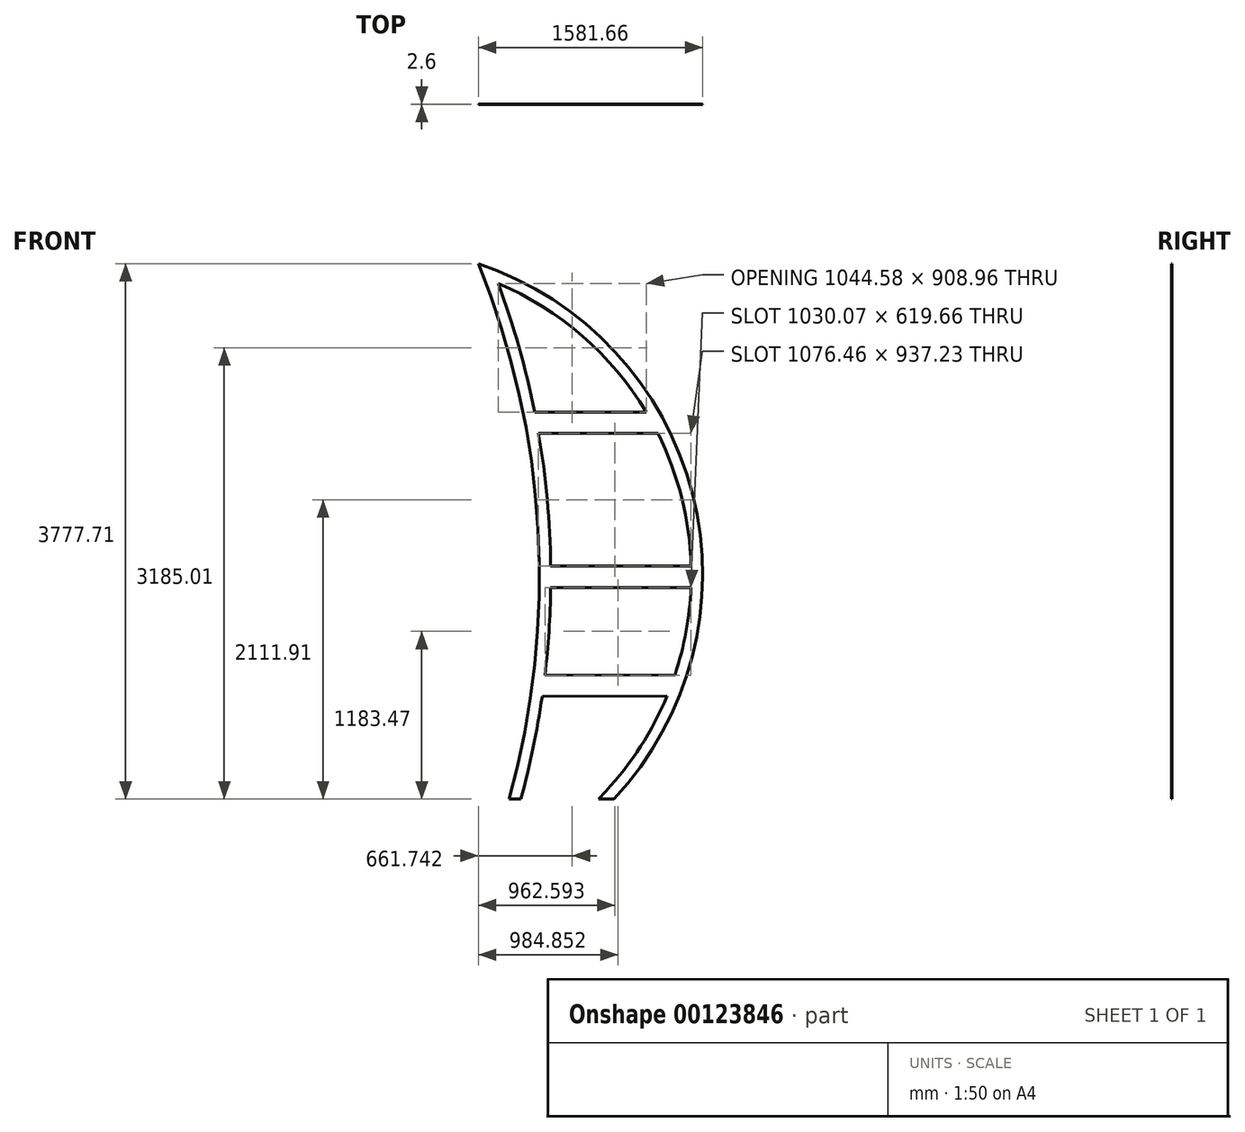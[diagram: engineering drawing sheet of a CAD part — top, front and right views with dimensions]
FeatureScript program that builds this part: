
annotation { "Feature Type Name" : "Feature", "Feature Type Description" : "" }
export const myFeature = defineFeature(function(context is Context, id is Id, definition is map)
    precondition{}
    {
        {
            var Q0;
            Q0=qCreatedBy(makeId("Front.planeOp"),FACE);
            var sketch = newSketch(context, id + "F0", { "sketchPlane" : qUnion([Q0])});
            skArc(sketch, "E0", {"start": v(-809.64, -1060.94) * mm, "mid": v(-605.41, 845.86) * mm, "end": v(-1026.5, 2716.77) * mm});
            skArc(sketch, "E1", {"start": v(-70.02, -1060.94) * mm, "mid": v(484.37, 1089.36) * mm, "end": v(-1026.5, 2716.77) * mm});
            skPoint(sketch, "E2.startSnap0", {"position": v(479.69, 526.9) * mm});
            skLineSegment(sketch, "E3", {"start": v(-809.64, -1060.94) * mm, "end": v(-731.35, -1060.94) * mm});
            skPoint(sketch, "E4.orphan", {"position": v(342.47, -333.9) * mm});
            skLineSegment(sketch, "E5.trimOffspring", {"start": v(-175, -1060.94) * mm, "end": v(-70.02, -1060.94) * mm});
            skPoint(sketch, "E6.orphan", {"position": v(552.9, 623.88) * mm});
            skPoint(sketch, "E7.orphan", {"position": v(552.9, 526.9) * mm});
            skLineSegment(sketch, "E8", {"start": v(-731.35, -1060.94) * mm, "end": v(-726.65, -1060.94) * mm});
            skArc(sketch, "E9.0", {"start": v(-732.55, -1082.34) * mm, "mid": v(-642.5, -712.35) * mm, "end": v(-576.3, -337.36) * mm});
            skArc(sketch, "E10.0", {"start": v(-128.41, -1006.26) * mm, "mid": v(118.4, -690.04) * mm, "end": v(304.7, -334.79) * mm});
            skLineSegment(sketch, "E11", {"start": v(-128.41, -1006.26) * mm, "end": v(-179.63, -1060.94) * mm});
            skLineSegment(sketch, "E12", {"start": v(-576.3, -337.36) * mm, "end": v(304.7, -334.79) * mm});
            skLineSegment(sketch, "E13.0", {"start": v(-556.68, -187.3) * mm, "end": v(360.76, -184.62) * mm});
            skLineSegment(sketch, "E14", {"start": v(-516.26, 432.36) * mm, "end": v(473.4, 432.36) * mm});
            skLineSegment(sketch, "E15.0", {"start": v(-516.2, 582.36) * mm, "end": v(474.33, 582.36) * mm});
            skLineSegment(sketch, "E16", {"start": v(-602.13, 1519.59) * mm, "end": v(239.76, 1519.59) * mm});
            skArc(sketch, "E17.trimOffspring", {"start": v(157.54, 1669.59) * mm, "mid": v(-292.57, 2207.02) * mm, "end": v(-887.04, 2578.55) * mm});
            skArc(sketch, "E18.trimOffspring", {"start": v(-629.95, 1669.59) * mm, "mid": v(-740.43, 2129.18) * mm, "end": v(-887.04, 2578.55) * mm});
            skLineSegment(sketch, "E19.trimOffspring", {"start": v(-629.95, 1669.59) * mm, "end": v(157.54, 1669.59) * mm});
            skArc(sketch, "E20.trimOffspring", {"start": v(-516.2, 582.36) * mm, "mid": v(-540.61, 1052.67) * mm, "end": v(-602.13, 1519.59) * mm});
            skArc(sketch, "E21.trimOffspring", {"start": v(474.33, 582.36) * mm, "mid": v(408.3, 1063.8) * mm, "end": v(239.76, 1519.59) * mm});
            skPoint(sketch, "E22.orphan", {"position": v(605.94, -333.9) * mm});
            skArc(sketch, "E23.trimOffspring", {"start": v(360.76, -184.62) * mm, "mid": v(438.83, 119.9) * mm, "end": v(473.4, 432.36) * mm});
            skArc(sketch, "E24.trimOffspring", {"start": v(-556.68, -187.3) * mm, "mid": v(-528.38, 122) * mm, "end": v(-516.26, 432.36) * mm});
            skLineSegment(sketch, "E25.trimOffspring", {"start": v(-179.63, -1060.94) * mm, "end": v(-175, -1060.94) * mm});
            skSolve(sketch);
        }
        {
            var Q0;
            Q0 = qSketchRegion(id + "F0", true);
            extrude(context, id + "F1", {"entities" : qUnion([Q0]), "depth" : 2.6 * mm, "offsetDistance" : 25 * mm});
        }
    });
